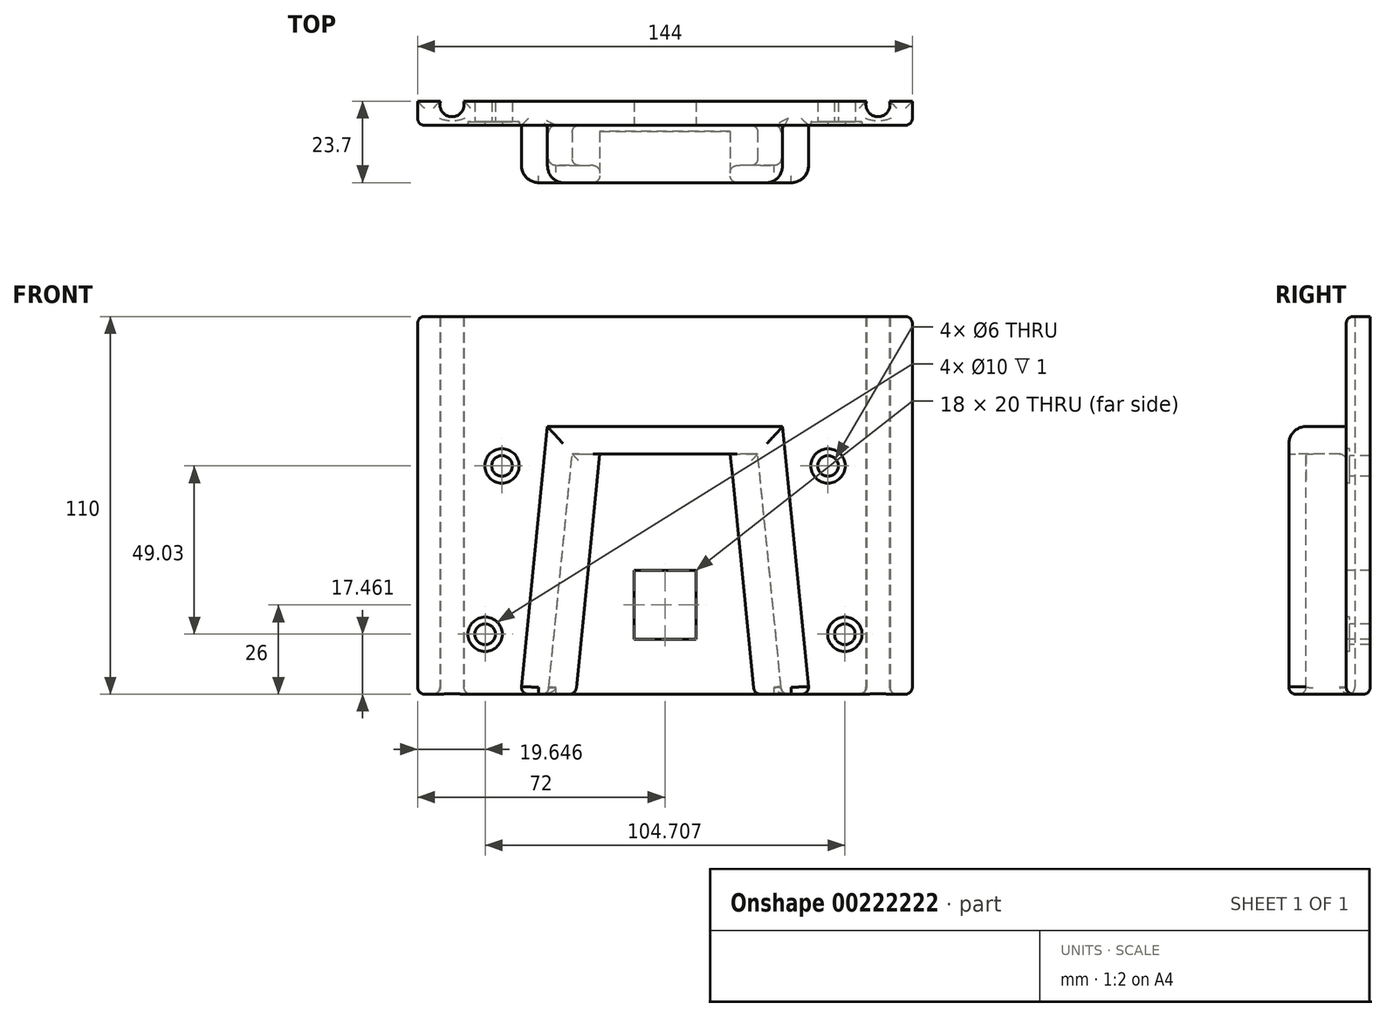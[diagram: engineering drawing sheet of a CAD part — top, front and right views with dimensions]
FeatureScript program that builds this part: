
annotation { "Feature Type Name" : "Feature", "Feature Type Description" : "" }
export const myFeature = defineFeature(function(context is Context, id is Id, definition is map)
    precondition{}
    {
        {
            var Q0;
            Q0=qCreatedBy(makeId("Front.planeOp"),FACE);
            var sketch = newSketch(context, id + "F0", { "sketchPlane" : qUnion([Q0])});
            skLineSegment(sketch, "E0.left", {"start": v(0, 0) * mm, "end": v(0, 0) * mm});
            skLineSegment(sketch, "E1", {"start": v(0, 0) * mm, "end": v(-72, 0) * mm});
            skLineSegment(sketch, "E2", {"start": v(-72, 0) * mm, "end": v(-72, 110) * mm});
            skLineSegment(sketch, "E3", {"start": v(-72, 110) * mm, "end": v(0, 110) * mm});
            skLineSegment(sketch, "E4", {"start": v(0, 102.01) * mm, "end": v(0, -45.63) * mm, "construction": true});
            skLineSegment(sketch, "E5", {"start": v(-34, 0) * mm, "end": v(-27, 70) * mm});
            skLineSegment(sketch, "E6", {"start": v(-27, 70) * mm, "end": v(0, 70) * mm});
            skLineSegment(sketch, "E7", {"start": v(0, 70) * mm, "end": v(2, 70) * mm});
            skPoint(sketch, "E8", {"position": v(-52.35, 17.46) * mm});
            skPoint(sketch, "E9", {"position": v(-47.45, 66.5) * mm});
            skSolve(sketch);
        }
        {
            var Q0;
            Q0=qCreatedBy(makeId("Top.planeOp"),FACE);
            var sketch = newSketch(context, id + "F1", { "sketchPlane" : qUnion([Q0])});
            skLineSegment(sketch, "E10", {"start": v(-34, 0) * mm, "end": v(-34, -11.7) * mm});
            skLineSegment(sketch, "E11", {"start": v(-34, -11.7) * mm, "end": v(-26, -11.7) * mm});
            skLineSegment(sketch, "E12", {"start": v(-26, -11.7) * mm, "end": v(-26, -16.7) * mm});
            skLineSegment(sketch, "E13", {"start": v(-26, -16.7) * mm, "end": v(-42, -16.7) * mm});
            skLineSegment(sketch, "E14", {"start": v(-42, -16.7) * mm, "end": v(-42, 0) * mm});
            skLineSegment(sketch, "E15", {"start": v(-42, 0) * mm, "end": v(-34, 0) * mm});
            skSolve(sketch);
        }
        {
            var Q0;
            Q0=makeQuery(id+"F1.imprint","IMPRINT",FACE,{"disambiguationData":[TD([[makeQuery(id+"F1.imprint","IMPRINT",EDGE,{"derivedFrom":sQuery(id+"F1.wireOp",EDGE,"E10")}),-1.0]])]});
            var Q1;
            Q1=sQuery(id+"F0.wireOp",EDGE,"E5");
            var Q2;
            Q2=sQuery(id+"F0.wireOp",EDGE,"E6");
            var Q3;
            Q3=sQuery(id+"F0.wireOp",EDGE,"E7");
            sweep(context, id + "F2", {"profiles" : qUnion([Q0]), "path" : qUnion([Q1, Q2, Q3])});
        }
        {
            var Q0;
            Q0=qCreatedBy(makeId("Front.planeOp"),FACE);
            var sketch = newSketch(context, id + "F3", { "sketchPlane" : qUnion([Q0])});
            skLineSegment(sketch, "E16.bottom", {"start": v(0, 110) * mm, "end": v(-72, 110) * mm});
            skLineSegment(sketch, "E16.top", {"start": v(0, 0) * mm, "end": v(-72, 0) * mm});
            skLineSegment(sketch, "E16.left", {"start": v(0, 110) * mm, "end": v(0, 0) * mm});
            skLineSegment(sketch, "E16.right", {"start": v(-72, 110) * mm, "end": v(-72, 0) * mm});
            skSolve(sketch);
        }
        {
            var Q0;
            Q0=qSketchRegion(id+"F3",true);
            var Q1;
            {var subQ3=sQuery(id+"F0.wireOp",EDGE,"E2");Q1=makeQuery(id+"F0.imprint","IMPRINT",FACE,{"disambiguationData":[TD([[makeQuery(id+"F0.imprint","IMPRINT",EDGE,{"derivedFrom":subQ3}),-1.0]])]});}
            extrude(context, id + "F4", {"entities" : qUnion([Q0, Q1]), "operationType" : NewBodyOperationType.ADD, "oppositeDirection" : true, "offsetDistance" : 25 * mm, "depth" : 7 * mm});
        }
        {
            var Q0;
            Q0=makeQuery(id+"F2.opSweep","SWEPT_EDGE",EDGE,{"disambiguationData":[OSD([sQuery(id+"F0.wireOp",EDGE,"E5"),sQuery(id+"F1.wireOp",EDGE,"E13"),sQuery(id+"F1.wireOp",EDGE,"E14")])]});
            var Q1;
            Q1=makeQuery(id+"F2.opSweep","SWEPT_EDGE",EDGE,{"disambiguationData":[OSD([sQuery(id+"F0.wireOp",EDGE,"E6"),sQuery(id+"F1.wireOp",EDGE,"E13"),sQuery(id+"F1.wireOp",EDGE,"E14")])]});
            var Q2;
            {var subQ0=sQuery(id+"F1.wireOp",EDGE,"E14");Q2=makeQuery(id+"F4.boolean.opBoolean","SPLIT",EDGE,{"disambiguationData":[topologyDisambiguationEdgeConnected([makeQuery(id+"F4.opExtrude","CAP_FACE",FACE,{"disambiguationData":[OSD([sQuery(id+"F3.wireOp",EDGE,"E16.bottom"),sQuery(id+"F3.wireOp",EDGE,"E16.top"),sQuery(id+"F3.wireOp",EDGE,"E16.left"),sQuery(id+"F3.wireOp",EDGE,"E16.right")])],"isStart":true})])],"derivedFrom":makeQuery(id+"F2.opSweep","SWEPT_EDGE",EDGE,{"disambiguationData":[OSD([sQuery(id+"F0.wireOp",EDGE,"E6"),subQ0,sQuery(id+"F1.wireOp",EDGE,"E15")])]})});}
            var Q3;
            Q3=makeQuery(id+"F2.opSweep","SWEPT_EDGE",EDGE,{"disambiguationData":[OSD([sQuery(id+"F0.wireOp",EDGE,"E5"),sQuery(id+"F1.wireOp",EDGE,"E14"),sQuery(id+"F1.wireOp",EDGE,"E15")])]});
            fillet(context, id + "F5", {"entities" : qUnion([Q0, Q1, Q2, Q3]), "radius" : 5 * mm, "tangentPropagation" : true, "allowEdgeOverflow" : false});
        }
        {
            var Q0;
            Q0=sQuery(id+"F0.wireOp",VERTEX,"E9");
            var Q1;
            Q1=sQuery(id+"F0.wireOp",VERTEX,"E8");
            var Q2;
            Q2=makeQuery(id+"F2.opSweep","SWEPT_BODY",BODY,{"disambiguationData":[OSD([sQuery(id+"F0.wireOp",EDGE,"E7"),sQuery(id+"F1.wireOp",EDGE,"E10"),sQuery(id+"F1.wireOp",EDGE,"E11"),sQuery(id+"F1.wireOp",EDGE,"E12"),sQuery(id+"F1.wireOp",EDGE,"E13"),sQuery(id+"F1.wireOp",EDGE,"E14"),sQuery(id+"F1.wireOp",EDGE,"E15")])]});
            hole(context, id + "F6", {"style" : HoleStyle.C_BORE, "endStyle" : HoleEndStyle.THROUGH, "holeDiameter" : 6 * mm, "cBoreDiameter" : 10 * mm, "cBoreDepth" : 1 * mm, "locations" : qUnion([Q0, Q1]), "scope" : qUnion([Q2]), "isTappedThrough" : true});
        }
        {
            var Q0;
            Q0=qCreatedBy(makeId("Front.planeOp"),FACE);
            var sketch = newSketch(context, id + "F7", { "sketchPlane" : qUnion([Q0])});
            skLineSegment(sketch, "E17.bottom", {"start": v(0, 36) * mm, "end": v(-9, 36) * mm});
            skLineSegment(sketch, "E17.top", {"start": v(0, 16) * mm, "end": v(-9, 16) * mm});
            skLineSegment(sketch, "E17.left", {"start": v(0, 36) * mm, "end": v(0, 16) * mm});
            skLineSegment(sketch, "E17.right", {"start": v(-9, 36) * mm, "end": v(-9, 16) * mm});
            skSolve(sketch);
        }
        {
            var Q0;
            Q0=makeQuery(id+"F7.imprint","IMPRINT",FACE,{"disambiguationData":[TD([[makeQuery(id+"F7.imprint","IMPRINT",EDGE,{"derivedFrom":sQuery(id+"F7.wireOp",EDGE,"E17.bottom")}),1.0]])]});
            extrude(context, id + "F8", {"entities" : qUnion([Q0]), "operationType" : NewBodyOperationType.REMOVE, "endBound" : BoundingType.THROUGH_ALL, "oppositeDirection" : true, "offsetDistance" : 25 * mm, "depth" : 6 * mm});
        }
        {
            var Q0;
            {var subQ0=makeQuery(id+"F2.opSweep","SWEPT_FACE",FACE,{"disambiguationData":[OSD([sQuery(id+"F0.wireOp",EDGE,"E5"),sQuery(id+"F1.wireOp",EDGE,"E13")])]});Q0=makeQuery(id+"F13.boolean.opBoolean","MERGE",FACE,{"derivedFrom":[subQ0,makeQuery(id+"F13.opPattern","COPY",FACE,{"derivedFrom":subQ0,"instanceName":"1"})]});}
            var sketch = newSketch(context, id + "F9", { "sketchPlane" : qUnion([Q0])});
            skLineSegment(sketch, "E18", {"start": v(-19.8, 62.04) * mm, "end": v(-18.98, 70.03) * mm});
            skLineSegment(sketch, "E19", {"start": v(-18.98, 70.03) * mm, "end": v(2, 70.03) * mm});
            skLineSegment(sketch, "E20", {"start": v(-19.8, 62.04) * mm, "end": v(2.8, 62.04) * mm});
            skSolve(sketch);
        }
        {
            var Q0;
            Q0=makeQuery(id+"F9.imprint","IMPRINT",FACE,{"disambiguationData":[TD([[makeQuery(id+"F9.imprint","IMPRINT",EDGE,{"derivedFrom":sQuery(id+"F9.wireOp",EDGE,"E18")}),-1.0]])]});
            extrude(context, id + "F10", {"entities" : qUnion([Q0]), "operationType" : NewBodyOperationType.REMOVE, "oppositeDirection" : true, "depth" : 15 * mm});
        }
        {
            var Q0;
            {var subQ0=makeQuery(id+"F4.boolean.opBoolean","MERGE",FACE,{"derivedFrom":[makeQuery(id+"F2.opSweep","CAP_FACE",FACE,{"disambiguationData":[OSD([sQuery(id+"F0.wireOp",VERTEX,"E5.start"),sQuery(id+"F1.wireOp",EDGE,"E10"),sQuery(id+"F1.wireOp",EDGE,"E11"),sQuery(id+"F1.wireOp",EDGE,"E12"),sQuery(id+"F1.wireOp",EDGE,"E13"),sQuery(id+"F1.wireOp",EDGE,"E14"),sQuery(id+"F1.wireOp",EDGE,"E15")])],"isStart":true}),makeQuery(id+"F4.opExtrude","SWEPT_FACE",FACE,{"disambiguationData":[OSD([sQuery(id+"F3.wireOp",EDGE,"E16.top")])]})]});Q0=makeQuery(id+"F13.boolean.opBoolean","MERGE",FACE,{"derivedFrom":[subQ0,makeQuery(id+"F13.opPattern","COPY",FACE,{"derivedFrom":subQ0,"instanceName":"1"})]});}
            var sketch = newSketch(context, id + "F11", { "sketchPlane" : qUnion([Q0])});
            skCircle(sketch, "E21", {"center": v(-62, -6) * mm, "radius": 3.5 * mm});
            skSolve(sketch);
        }
        {
            var Q0;
            {var subQ0=sQuery(id+"F11.wireOp",EDGE,"E21");var subQ1=makeQuery(id+"F4.opExtrude","CAP_EDGE",EDGE,{"disambiguationData":[OSD([sQuery(id+"F3.wireOp",EDGE,"E16.top")])],"isStart":false});var subQ2=makeQuery(id+"F11.imprint","INTERSECT",VERTEX,{"disambiguationData":[OD(0.0)],"derivedFrom":[subQ1,subQ0]});Q0=makeQuery(id+"F11.imprint","IMPRINT",FACE,{"disambiguationData":[TD([[makeQuery(id+"F11.imprint","IMPRINT",EDGE,{"disambiguationData":[TD([[subQ2,-1.0]])],"derivedFrom":subQ0}),1.0]])]});}
            var Q1;
            Q1=sQuery(id+"F11.wireOp",EDGE,"E21");
            extrude(context, id + "F12", {"entities" : qUnion([Q0]), "operationType" : NewBodyOperationType.REMOVE, "surfaceEntities" : qUnion([Q1]), "oppositeDirection" : true, "depth" : 200 * mm});
        }
        {
            var Q0;
            Q0=makeQuery(id+"F2.opSweep","SWEPT_BODY",BODY,{"disambiguationData":[OSD([sQuery(id+"F0.wireOp",EDGE,"E7"),sQuery(id+"F1.wireOp",EDGE,"E10"),sQuery(id+"F1.wireOp",EDGE,"E11"),sQuery(id+"F1.wireOp",EDGE,"E12"),sQuery(id+"F1.wireOp",EDGE,"E13"),sQuery(id+"F1.wireOp",EDGE,"E14"),sQuery(id+"F1.wireOp",EDGE,"E15")])]});
            var Q1;
            Q1=qCreatedBy(makeId("Right.planeOp"),FACE);
            mirror(context, id + "F13", {"operationType" : NewBodyOperationType.ADD, "entities" : qUnion([Q0]), "mirrorPlane" : qUnion([Q1])});
        }
        {
            var Q0;
            Q0=makeQuery(id+"F2.opSweep","SWEPT_EDGE",EDGE,{"disambiguationData":[OSD([sQuery(id+"F0.wireOp",EDGE,"E5"),sQuery(id+"F1.wireOp",EDGE,"E10"),sQuery(id+"F1.wireOp",EDGE,"E11")])]});
            var Q1;
            {var subQ0=makeQuery(id+"F4.boolean.opBoolean","MERGE",FACE,{"derivedFrom":[makeQuery(id+"F2.opSweep","CAP_FACE",FACE,{"disambiguationData":[OSD([sQuery(id+"F0.wireOp",VERTEX,"E5.start"),sQuery(id+"F1.wireOp",EDGE,"E10"),sQuery(id+"F1.wireOp",EDGE,"E11"),sQuery(id+"F1.wireOp",EDGE,"E12"),sQuery(id+"F1.wireOp",EDGE,"E13"),sQuery(id+"F1.wireOp",EDGE,"E14"),sQuery(id+"F1.wireOp",EDGE,"E15")])],"isStart":true}),makeQuery(id+"F4.opExtrude","SWEPT_FACE",FACE,{"disambiguationData":[OSD([sQuery(id+"F3.wireOp",EDGE,"E16.top")])]})]});Q1=makeQuery(id+"F13.boolean.opBoolean","MERGE",FACE,{"derivedFrom":[subQ0,makeQuery(id+"F13.opPattern","COPY",FACE,{"derivedFrom":subQ0,"instanceName":"1"})]});}
            var Q2;
            Q2=makeQuery(id+"F13.opPattern","COPY",EDGE,{"derivedFrom":makeQuery(id+"F2.opSweep","SWEPT_EDGE",EDGE,{"disambiguationData":[OSD([sQuery(id+"F0.wireOp",EDGE,"E5"),sQuery(id+"F1.wireOp",EDGE,"E10"),sQuery(id+"F1.wireOp",EDGE,"E11")])]}),"instanceName":"1"});
            var Q3;
            Q3=makeQuery(id+"F2.opSweep","SWEPT_EDGE",EDGE,{"disambiguationData":[OSD([sQuery(id+"F0.wireOp",EDGE,"E5"),sQuery(id+"F1.wireOp",EDGE,"E12"),sQuery(id+"F1.wireOp",EDGE,"E13")])]});
            var Q4;
            {var subQ0=makeQuery(id+"F2.opSweep","SWEPT_EDGE",EDGE,{"disambiguationData":[OSD([sQuery(id+"F0.wireOp",EDGE,"E6"),sQuery(id+"F1.wireOp",EDGE,"E12"),sQuery(id+"F1.wireOp",EDGE,"E13")])]});Q4=makeQuery(id+"F13.boolean.opBoolean","MERGE",EDGE,{"derivedFrom":[subQ0,makeQuery(id+"F13.opPattern","COPY",EDGE,{"derivedFrom":subQ0,"instanceName":"1"})]});}
            var Q5;
            Q5=makeQuery(id+"F13.opPattern","COPY",EDGE,{"derivedFrom":makeQuery(id+"F2.opSweep","SWEPT_EDGE",EDGE,{"disambiguationData":[OSD([sQuery(id+"F0.wireOp",EDGE,"E5"),sQuery(id+"F1.wireOp",EDGE,"E12"),sQuery(id+"F1.wireOp",EDGE,"E13")])]}),"instanceName":"1"});
            var Q6;
            Q6=makeQuery(id+"F2.opSweep","SWEPT_EDGE",EDGE,{"disambiguationData":[OSD([sQuery(id+"F0.wireOp",EDGE,"E5"),sQuery(id+"F1.wireOp",EDGE,"E11"),sQuery(id+"F1.wireOp",EDGE,"E12")])]});
            var Q7;
            {var subQ0=makeQuery(id+"F2.opSweep","SWEPT_EDGE",EDGE,{"disambiguationData":[OSD([sQuery(id+"F0.wireOp",EDGE,"E6"),sQuery(id+"F1.wireOp",EDGE,"E11"),sQuery(id+"F1.wireOp",EDGE,"E12")])]});Q7=makeQuery(id+"F13.boolean.opBoolean","MERGE",EDGE,{"derivedFrom":[subQ0,makeQuery(id+"F13.opPattern","COPY",EDGE,{"derivedFrom":subQ0,"instanceName":"1"})]});}
            var Q8;
            Q8=makeQuery(id+"F13.opPattern","COPY",EDGE,{"derivedFrom":makeQuery(id+"F2.opSweep","SWEPT_EDGE",EDGE,{"disambiguationData":[OSD([sQuery(id+"F0.wireOp",EDGE,"E5"),sQuery(id+"F1.wireOp",EDGE,"E11"),sQuery(id+"F1.wireOp",EDGE,"E12")])]}),"instanceName":"1"});
            var Q9;
            Q9=makeQuery(id+"F4.opExtrude","SWEPT_EDGE",EDGE,{"disambiguationData":[OSD([sQuery(id+"F3.wireOp",EDGE,"E16.bottom"),sQuery(id+"F3.wireOp",EDGE,"E16.right")])]});
            var Q10;
            Q10=makeQuery(id+"F13.opPattern","COPY",EDGE,{"derivedFrom":makeQuery(id+"F4.opExtrude","SWEPT_EDGE",EDGE,{"disambiguationData":[OSD([sQuery(id+"F3.wireOp",EDGE,"E16.bottom"),sQuery(id+"F3.wireOp",EDGE,"E16.right")])]}),"instanceName":"1"});
            fillet(context, id + "F14", {"entities" : qUnion([Q0, Q1, Q2, Q3, Q4, Q5, Q6, Q7, Q8, Q9, Q10]), "radius" : 2 * mm, "tangentPropagation" : true, "allowEdgeOverflow" : false});
        }
        {
            var Q0;
            Q0=makeQuery(id+"F4.opExtrude","CAP_EDGE",EDGE,{"disambiguationData":[OSD([sQuery(id+"F3.wireOp",EDGE,"E16.right")])],"isStart":true});
            var Q1;
            {var subQ0=makeQuery(id+"F10.boolean.opBoolean","COPY",EDGE,{"derivedFrom":makeQuery(id+"F10.opExtrude","CAP_EDGE",EDGE,{"disambiguationData":[OSD([sQuery(id+"F9.wireOp",EDGE,"E19")])],"isStart":true})});Q1=makeQuery(id+"F13.boolean.opBoolean","MERGE",EDGE,{"derivedFrom":[subQ0,makeQuery(id+"F13.opPattern","COPY",EDGE,{"derivedFrom":subQ0,"instanceName":"1"})]});}
            var Q2;
            Q2=makeQuery(id+"F2.opSweep","SWEPT_EDGE",EDGE,{"disambiguationData":[OSD([sQuery(id+"F0.wireOp",EDGE,"E5"),sQuery(id+"F1.wireOp",EDGE,"E10"),sQuery(id+"F1.wireOp",EDGE,"E15")])]});
            var Q3;
            {var subQ0=sQuery(id+"F1.wireOp",EDGE,"E10");var subQ2=sQuery(id+"F1.wireOp",EDGE,"E15");var subQ3=makeQuery(id+"F2.opSweep","SWEPT_EDGE",EDGE,{"disambiguationData":[OSD([sQuery(id+"F0.wireOp",EDGE,"E6"),subQ0,subQ2])]});var subQ4=makeQuery(id+"F4.boolean.opBoolean","SPLIT",EDGE,{"disambiguationData":[topologyDisambiguationEdgeConnected([makeQuery(id+"F4.opExtrude","CAP_FACE",FACE,{"disambiguationData":[OSD([sQuery(id+"F3.wireOp",EDGE,"E16.bottom"),sQuery(id+"F3.wireOp",EDGE,"E16.top"),sQuery(id+"F3.wireOp",EDGE,"E16.left"),sQuery(id+"F3.wireOp",EDGE,"E16.right")])],"isStart":true})])],"derivedFrom":subQ3});Q3=makeQuery(id+"F13.boolean.opBoolean","MERGE",EDGE,{"derivedFrom":[makeQuery(id+"F4.boolean.opBoolean","SPLIT",EDGE,{"disambiguationData":[topologyDisambiguationEdgeConnected([makeQuery(id+"F2.opSweep","SWEPT_FACE",FACE,{"disambiguationData":[OSD([sQuery(id+"F0.wireOp",EDGE,"E5"),subQ2])]})])],"derivedFrom":subQ3}),subQ4,makeQuery(id+"F13.opPattern","COPY",EDGE,{"derivedFrom":subQ4,"instanceName":"1"})]});}
            var Q4;
            Q4=makeQuery(id+"F13.opPattern","COPY",EDGE,{"derivedFrom":makeQuery(id+"F2.opSweep","SWEPT_EDGE",EDGE,{"disambiguationData":[OSD([sQuery(id+"F0.wireOp",EDGE,"E5"),sQuery(id+"F1.wireOp",EDGE,"E10"),sQuery(id+"F1.wireOp",EDGE,"E15")])]}),"instanceName":"1"});
            fillet(context, id + "F15", {"entities" : qUnion([Q0, Q1, Q2, Q3, Q4]), "radius" : 2 * mm, "tangentPropagation" : true, "allowEdgeOverflow" : false});
        }
    });
